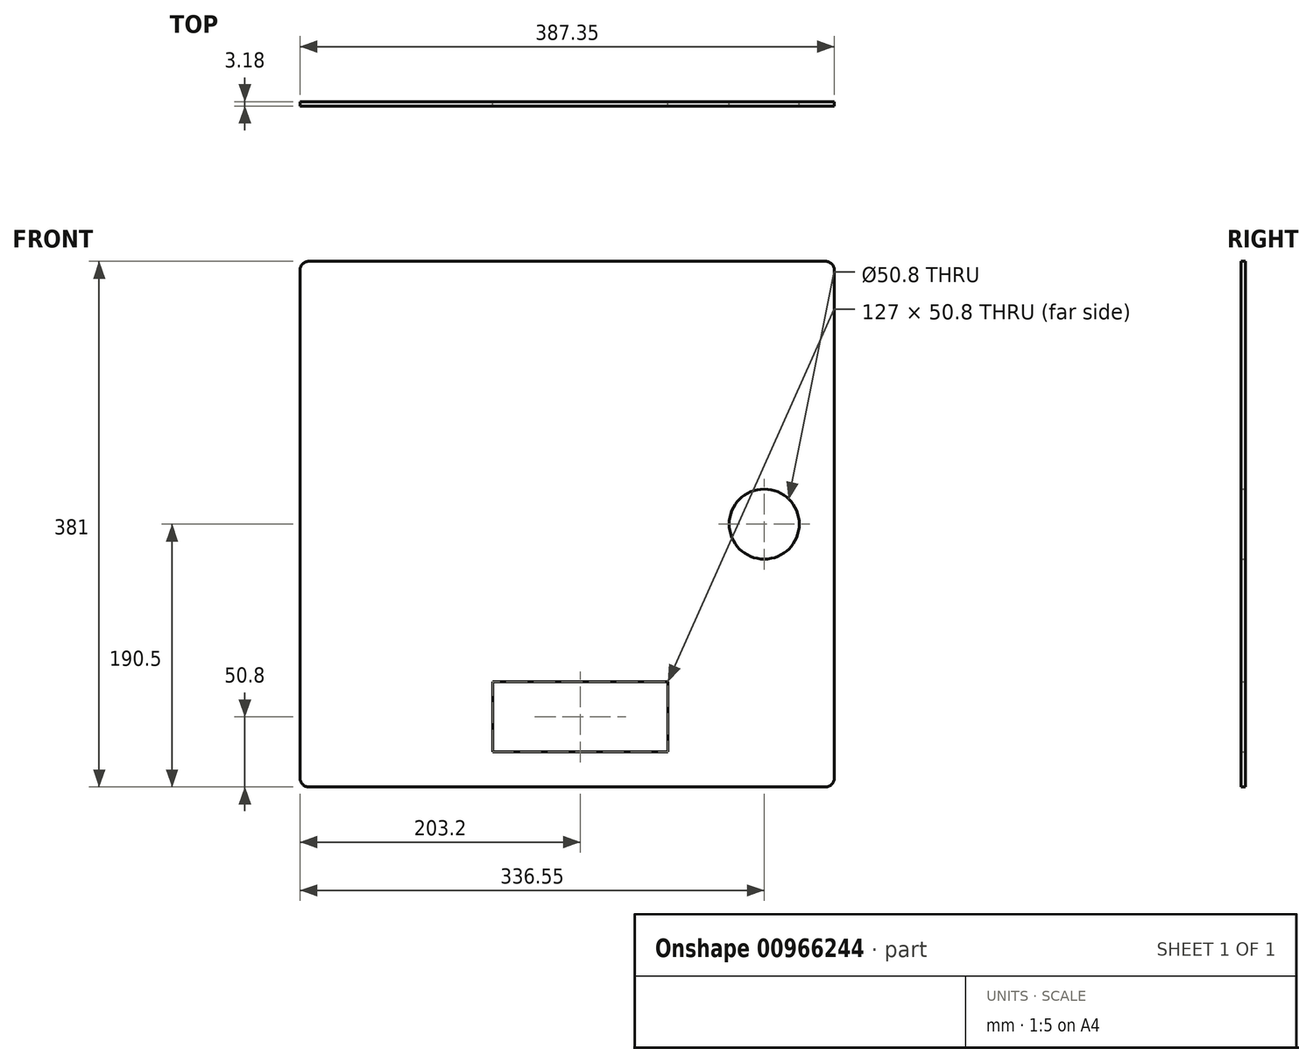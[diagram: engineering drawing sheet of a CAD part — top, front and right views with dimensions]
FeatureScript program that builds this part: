
annotation { "Feature Type Name" : "Feature", "Feature Type Description" : "" }
export const myFeature = defineFeature(function(context is Context, id is Id, definition is map)
    precondition{}
    {
        {
            var Q0;
            Q0=qCreatedBy(makeId("Front.planeOp"),FACE);
            var sketch = newSketch(context, id + "F0", { "sketchPlane" : qUnion([Q0])});
            skLineSegment(sketch, "E0.bottom", {"start": v(6.35, 0) * mm, "end": v(381, 0) * mm});
            skLineSegment(sketch, "E0.top", {"start": v(6.35, 381) * mm, "end": v(381, 381) * mm});
            skLineSegment(sketch, "E0.left", {"start": v(0, 6.35) * mm, "end": v(0, 374.65) * mm});
            skLineSegment(sketch, "E0.right", {"start": v(387.35, 6.35) * mm, "end": v(387.35, 374.65) * mm});
            skPoint(sketch, "E1.visualSharp", {"position": v(0, 381) * mm});
            skArc(sketch, "E1.filletArc", {"start": v(6.35, 381) * mm, "mid": v(1.86, 379.14) * mm, "end": v(0, 374.65) * mm});
            skPoint(sketch, "E2.visualSharp", {"position": v(0, 0) * mm});
            skArc(sketch, "E2.filletArc", {"start": v(0, 6.35) * mm, "mid": v(1.86, 1.86) * mm, "end": v(6.35, 0) * mm});
            skPoint(sketch, "E3.visualSharp", {"position": v(387.35, 0) * mm});
            skArc(sketch, "E3.filletArc", {"start": v(381, 0) * mm, "mid": v(385.5, 1.86) * mm, "end": v(387.35, 6.35) * mm});
            skPoint(sketch, "E4.visualSharp", {"position": v(387.35, 381) * mm});
            skArc(sketch, "E4.filletArc", {"start": v(387.35, 374.65) * mm, "mid": v(385.5, 379.14) * mm, "end": v(381, 381) * mm});
            skLineSegment(sketch, "E5.bottom", {"start": v(139.7, 76.2) * mm, "end": v(266.7, 76.2) * mm});
            skLineSegment(sketch, "E5.top", {"start": v(139.7, 25.4) * mm, "end": v(266.7, 25.4) * mm});
            skLineSegment(sketch, "E5.left", {"start": v(139.7, 76.2) * mm, "end": v(139.7, 25.4) * mm});
            skLineSegment(sketch, "E5.right", {"start": v(266.7, 76.2) * mm, "end": v(266.7, 25.4) * mm});
            skCircle(sketch, "E6", {"center": v(336.55, 190.5) * mm, "radius": 25.4 * mm});
            skSolve(sketch);
        }
        {
            var Q0;
            Q0=makeQuery(id+"F0.imprint","IMPRINT",FACE,{"disambiguationData":[TD([[makeQuery(id+"F0.imprint","IMPRINT",EDGE,{"derivedFrom":sQuery(id+"F0.wireOp",EDGE,"E0.bottom")}),1.0]])]});
            extrude(context, id + "F1", {"entities" : qUnion([Q0]), "depth" : 3.17 * mm});
        }
    });
